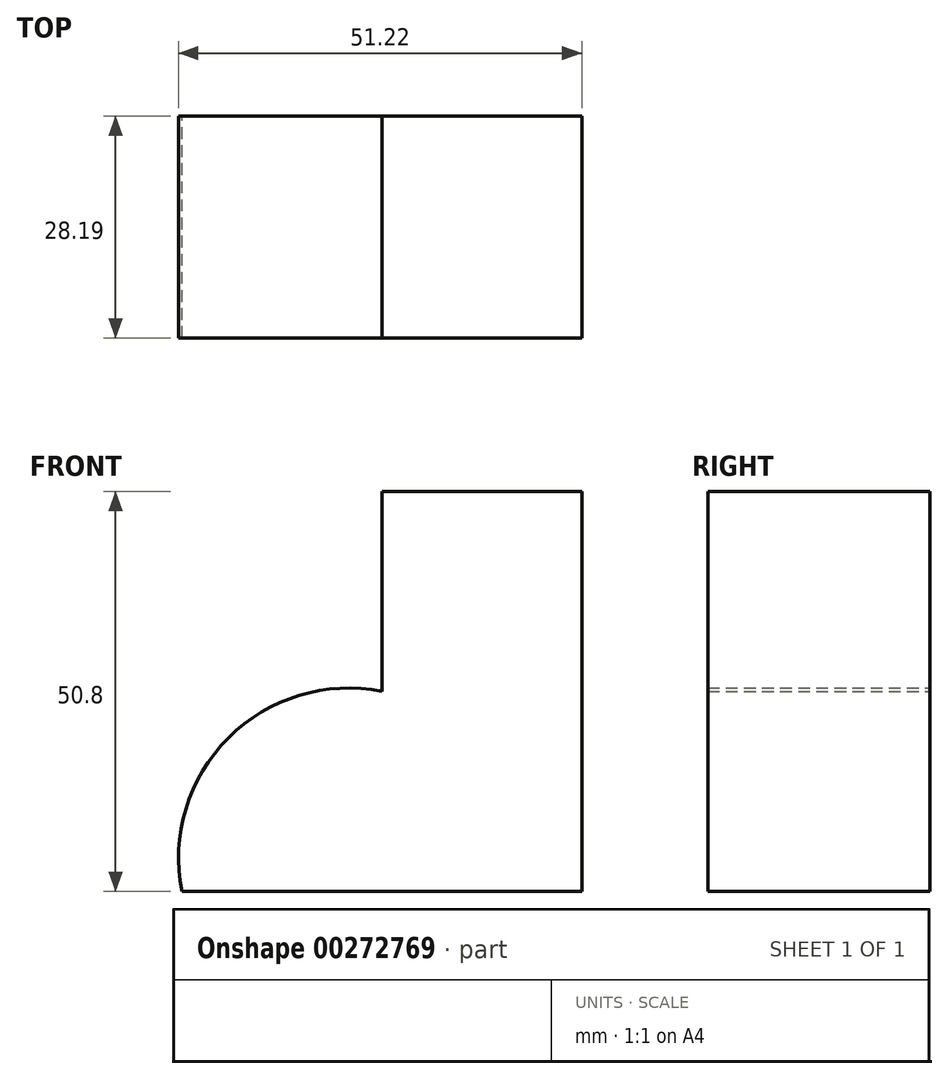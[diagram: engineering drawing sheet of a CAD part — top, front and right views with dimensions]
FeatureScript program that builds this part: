
annotation { "Feature Type Name" : "Feature", "Feature Type Description" : "" }
export const myFeature = defineFeature(function(context is Context, id is Id, definition is map)
    precondition{}
    {
        {
            var Q0;
            Q0=qCreatedBy(makeId("Front.planeOp"),FACE);
            var sketch = newSketch(context, id + "F0", { "sketchPlane" : qUnion([Q0])});
            skLineSegment(sketch, "E0", {"start": v(-23.7, 43.23) * mm, "end": v(1.7, 43.23) * mm});
            skLineSegment(sketch, "E1", {"start": v(1.7, 43.23) * mm, "end": v(1.7, -7.57) * mm});
            skLineSegment(sketch, "E2", {"start": v(1.7, -7.57) * mm, "end": v(-49.1, -7.57) * mm});
            skLineSegment(sketch, "E3", {"start": v(-23.7, 43.23) * mm, "end": v(-23.7, 17.83) * mm});
            skArc(sketch, "E4", {"start": v(-23.7, 17.83) * mm, "mid": v(-43.2, 11.93) * mm, "end": v(-49.1, -7.57) * mm});
            skSolve(sketch);
        }
        {
            var Q0;
            Q0=makeQuery(id+"F0.imprint","IMPRINT",FACE,{"disambiguationData":[TD([[makeQuery(id+"F0.imprint","IMPRINT",EDGE,{"derivedFrom":sQuery(id+"F0.wireOp",EDGE,"E0")}),-1.0]])]});
            extrude(context, id + "F1", {"entities" : qUnion([Q0]), "depth" : 28.2 * mm});
        }
    });
